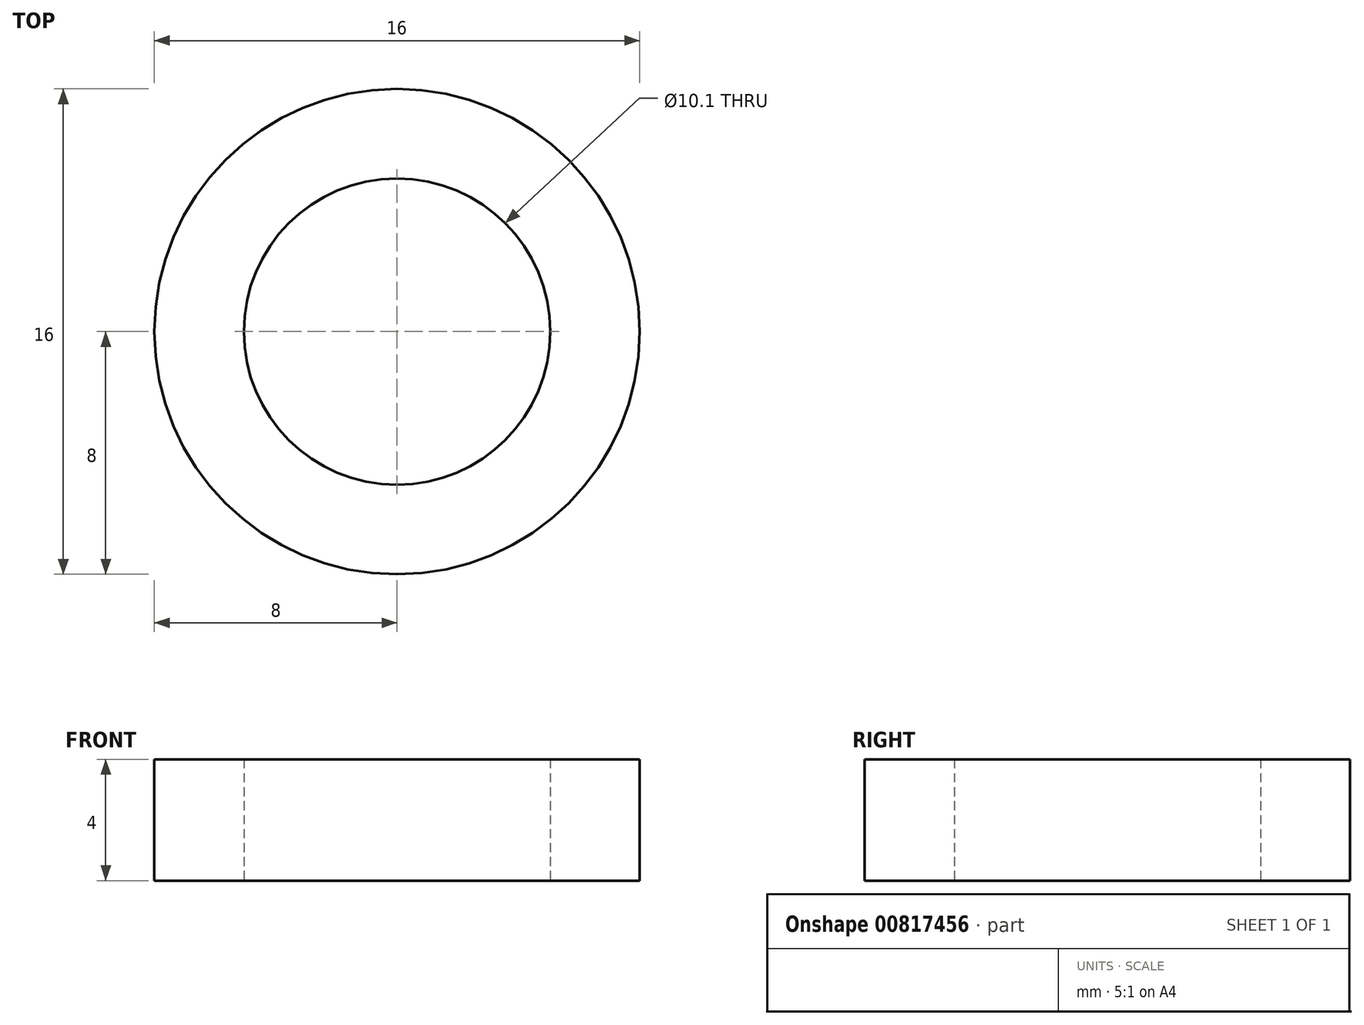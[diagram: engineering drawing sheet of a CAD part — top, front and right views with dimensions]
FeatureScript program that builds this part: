
annotation { "Feature Type Name" : "Feature", "Feature Type Description" : "" }
export const myFeature = defineFeature(function(context is Context, id is Id, definition is map)
    precondition{}
    {
        {
            var Q0;
            Q0=qCreatedBy(makeId("Top.planeOp"),FACE);
            var sketch = newSketch(context, id + "F0", { "sketchPlane" : qUnion([Q0])});
            skCircle(sketch, "E0", {"center": v(0, 0) * mm, "radius": 5.05 * mm});
            skCircle(sketch, "E1", {"center": v(0, 0) * mm, "radius": 8 * mm});
            skSolve(sketch);
        }
        {
            var Q0;
            Q0=makeQuery(id+"F0.imprint","IMPRINT",FACE,{"disambiguationData":[TD([[makeQuery(id+"F0.imprint","IMPRINT",EDGE,{"derivedFrom":sQuery(id+"F0.wireOp",EDGE,"E0")}),-1.0]])]});
            extrude(context, id + "F1", {"entities" : qUnion([Q0]), "depth" : 4 * mm, "offsetDistance" : 25 * mm});
        }
    });
